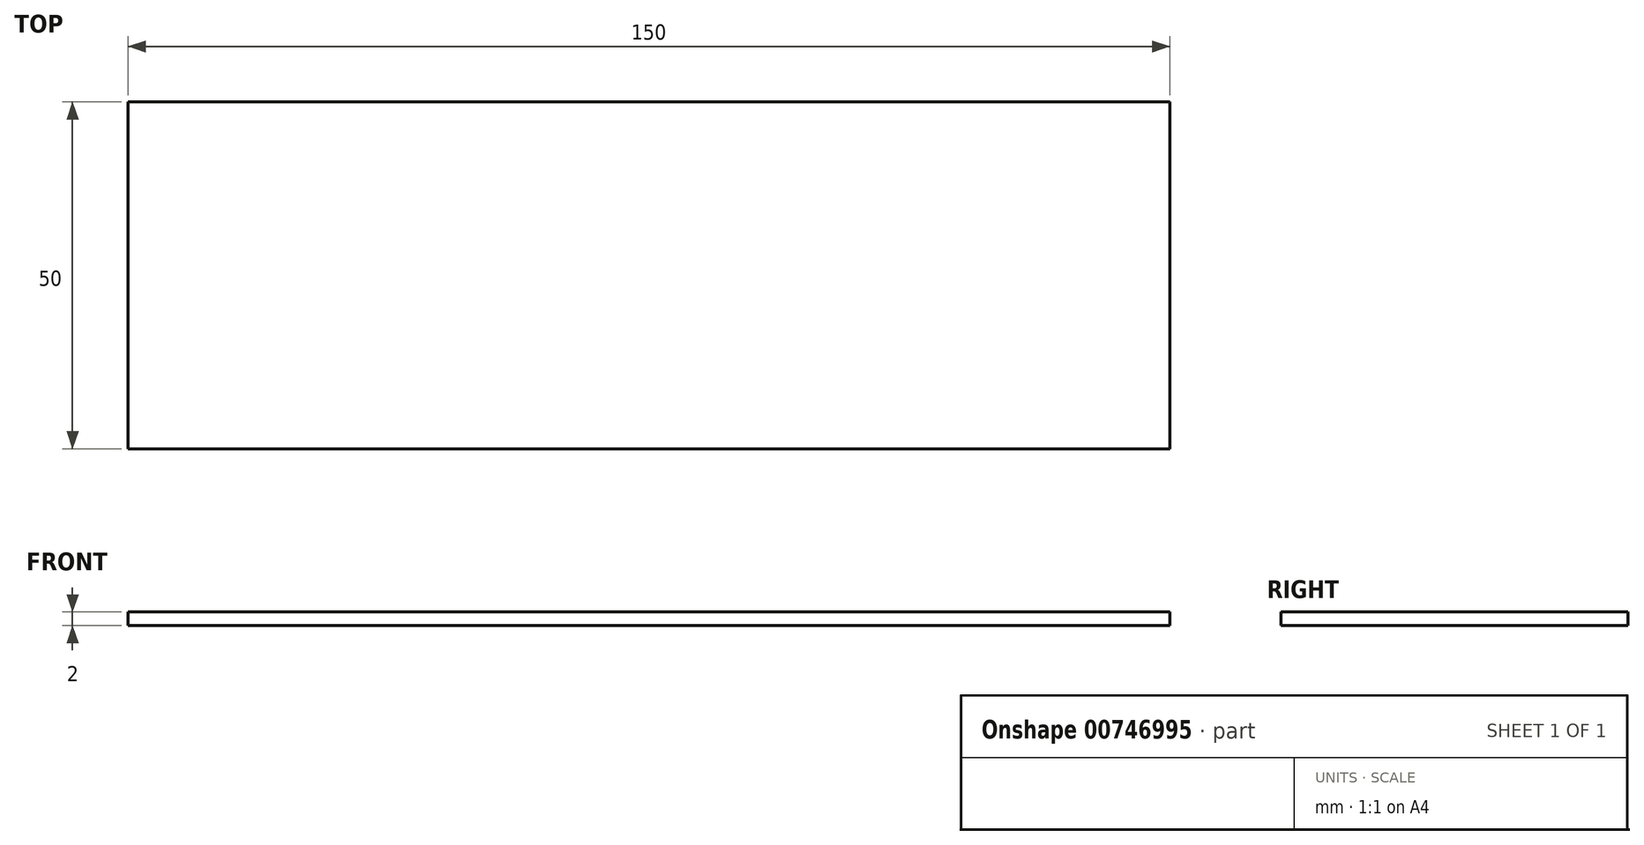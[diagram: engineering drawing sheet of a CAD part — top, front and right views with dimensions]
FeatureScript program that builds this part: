
annotation { "Feature Type Name" : "Feature", "Feature Type Description" : "" }
export const myFeature = defineFeature(function(context is Context, id is Id, definition is map)
    precondition{}
    {
        {
            var Q0;
            Q0=qCreatedBy(makeId("Top.planeOp"),FACE);
            var sketch = newSketch(context, id + "F0", { "sketchPlane" : qUnion([Q0])});
            skLineSegment(sketch, "E0.bottom", {"start": v(-67.57, 75.6) * mm, "end": v(82.43, 75.6) * mm});
            skLineSegment(sketch, "E0.top", {"start": v(-67.57, 25.6) * mm, "end": v(82.43, 25.6) * mm});
            skLineSegment(sketch, "E0.left", {"start": v(-67.57, 75.6) * mm, "end": v(-67.57, 25.6) * mm});
            skLineSegment(sketch, "E0.right", {"start": v(82.43, 75.6) * mm, "end": v(82.43, 25.6) * mm});
            skSolve(sketch);
        }
        {
            var Q0;
            Q0=makeQuery(id+"F0.imprint","IMPRINT",FACE,{"disambiguationData":[TD([[makeQuery(id+"F0.imprint","IMPRINT",EDGE,{"derivedFrom":sQuery(id+"F0.wireOp",EDGE,"E0.bottom")}),-1.0]])]});
            extrude(context, id + "F1", {"entities" : qUnion([Q0]), "depth" : 2 * mm, "offsetDistance" : 25 * mm});
        }
    });
